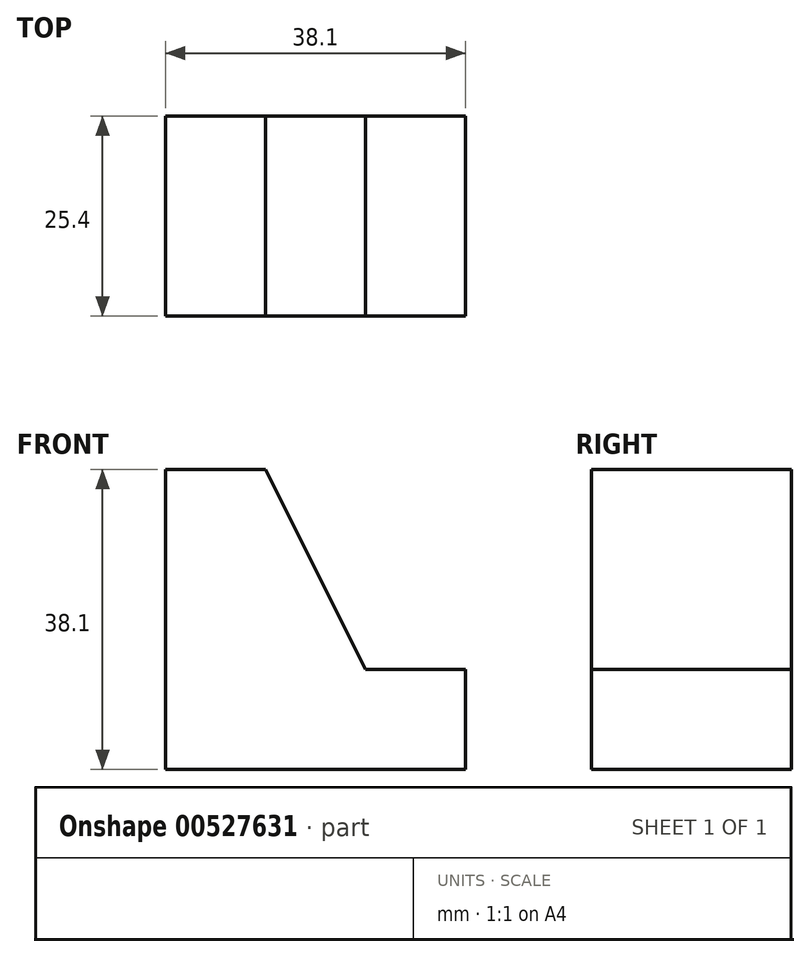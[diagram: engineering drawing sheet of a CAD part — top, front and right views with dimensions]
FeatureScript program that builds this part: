
annotation { "Feature Type Name" : "Feature", "Feature Type Description" : "" }
export const myFeature = defineFeature(function(context is Context, id is Id, definition is map)
    precondition{}
    {
        {
            var Q0;
            Q0=qCreatedBy(makeId("Front.planeOp"),FACE);
            var sketch = newSketch(context, id + "F0", { "sketchPlane" : qUnion([Q0])});
            skLineSegment(sketch, "E0", {"start": v(0, 0) * mm, "end": v(38.1, 0) * mm});
            skLineSegment(sketch, "E1", {"start": v(0, 0) * mm, "end": v(0, 38.1) * mm});
            skLineSegment(sketch, "E2", {"start": v(0, 38.1) * mm, "end": v(38.1, 38.1) * mm});
            skLineSegment(sketch, "E3", {"start": v(38.1, 38.1) * mm, "end": v(38.1, 0) * mm});
            skSolve(sketch);
        }
        {
            var Q0;
            Q0 = qSketchRegion(id + "F0", true);
            extrude(context, id + "F1", {"entities" : qUnion([Q0]), "depth" : 25.4 * mm, "offsetDistance" : 25.4 * mm});
        }
        {
            var Q0;
            Q0=makeQuery(id+"F1.opExtrude","CAP_FACE",FACE,{"disambiguationData":[OSD([sQuery(id+"F0.wireOp",EDGE,"E0"),sQuery(id+"F0.wireOp",EDGE,"E1"),sQuery(id+"F0.wireOp",EDGE,"E2"),sQuery(id+"F0.wireOp",EDGE,"E3")])],"isStart":false});
            var sketch = newSketch(context, id + "F2", { "sketchPlane" : qUnion([Q0])});
            skLineSegment(sketch, "E4", {"start": v(38.1, 12.7) * mm, "end": v(25.4, 12.7) * mm});
            skLineSegment(sketch, "E5", {"start": v(25.4, 12.7) * mm, "end": v(12.7, 38.1) * mm});
            skSolve(sketch);
        }
        {
            var Q0;
            {var subQ0=sQuery(id+"F2.wireOp",EDGE,"E4");Q0=makeQuery(id+"F2.imprint","IMPRINT",FACE,{"disambiguationData":[TD([[makeQuery(id+"F2.imprint","IMPRINT",EDGE,{"derivedFrom":subQ0}),-1.0]])]});}
            extrude(context, id + "F3", {"entities" : qUnion([Q0]), "operationType" : NewBodyOperationType.REMOVE, "oppositeDirection" : true, "depth" : 25.4 * mm, "offsetDistance" : 25.4 * mm});
        }
    });
